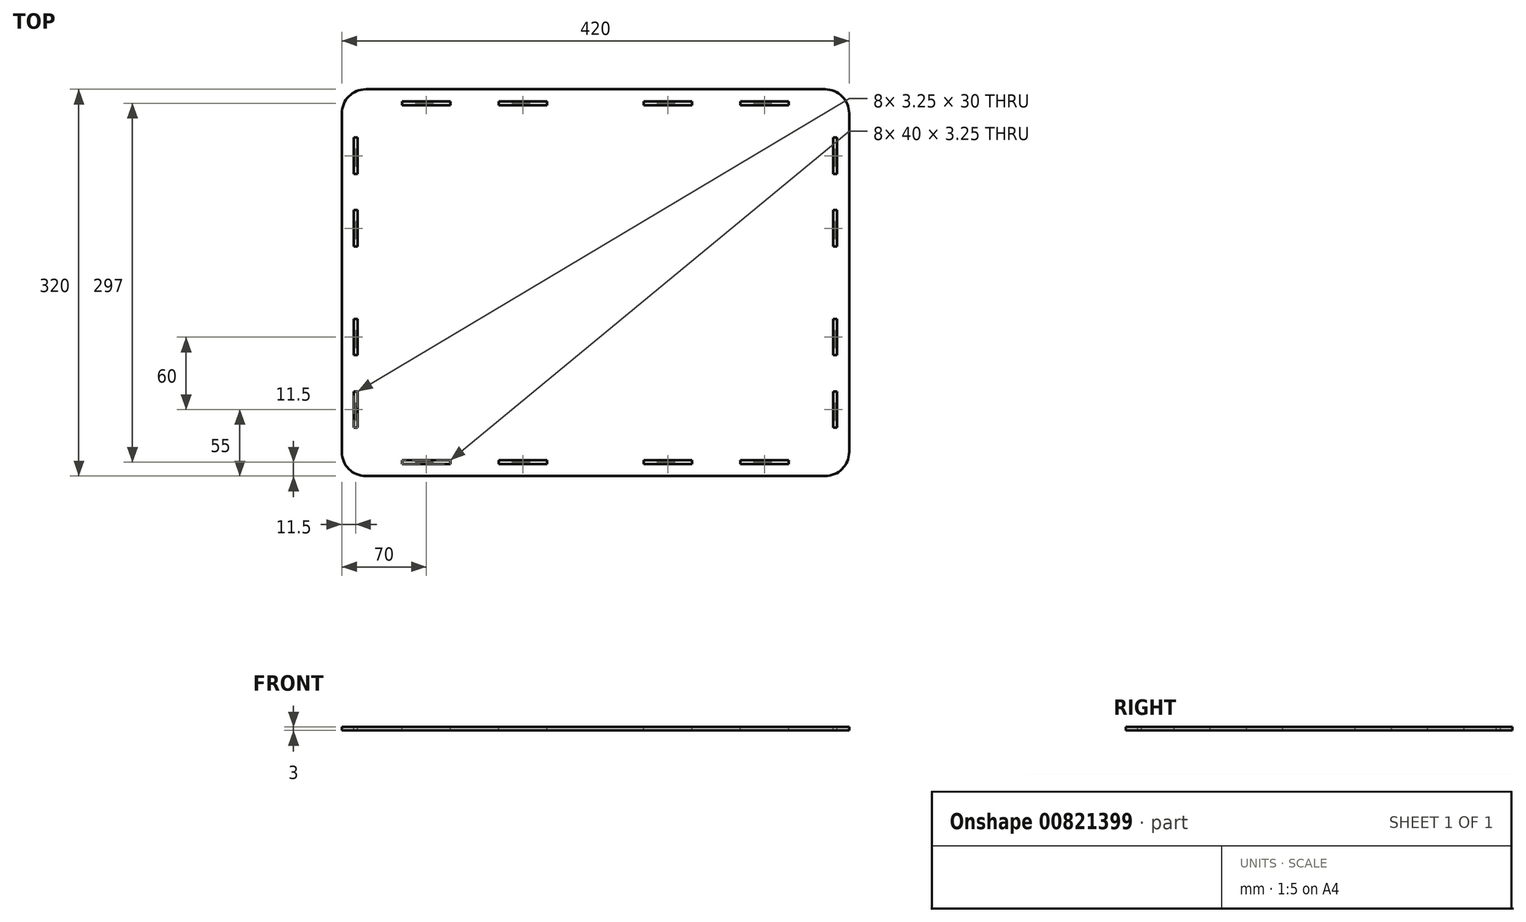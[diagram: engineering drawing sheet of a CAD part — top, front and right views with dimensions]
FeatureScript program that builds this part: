
annotation { "Feature Type Name" : "Feature", "Feature Type Description" : "" }
export const myFeature = defineFeature(function(context is Context, id is Id, definition is map)
    precondition{}
    {
        {
            var Q0;
            Q0=qCreatedBy(makeId("Top.planeOp"),FACE);
            var sketch = newSketch(context, id + "F0", { "sketchPlane" : qUnion([Q0])});
            skLineSegment(sketch, "E0.bottom", {"start": v(-190, 160) * mm, "end": v(190, 160) * mm});
            skLineSegment(sketch, "E0.top", {"start": v(-190, -160) * mm, "end": v(190, -160) * mm});
            skLineSegment(sketch, "E0.left", {"start": v(-210, 140) * mm, "end": v(-210, -140) * mm});
            skLineSegment(sketch, "E0.right", {"start": v(210, 140) * mm, "end": v(210, -140) * mm});
            skPoint(sketch, "E0.middle", {"position": v(0, 0) * mm});
            skPoint(sketch, "E1.visualSharp", {"position": v(210, 160) * mm});
            skArc(sketch, "E1.filletArc", {"start": v(210, 140) * mm, "mid": v(204.14, 154.14) * mm, "end": v(190, 160) * mm});
            skPoint(sketch, "E2.visualSharp", {"position": v(210, -160) * mm});
            skArc(sketch, "E2.filletArc", {"start": v(190, -160) * mm, "mid": v(204.14, -154.14) * mm, "end": v(210, -140) * mm});
            skPoint(sketch, "E3.visualSharp", {"position": v(-210, -160) * mm});
            skArc(sketch, "E3.filletArc", {"start": v(-210, -140) * mm, "mid": v(-204.14, -154.14) * mm, "end": v(-190, -160) * mm});
            skPoint(sketch, "E4.visualSharp", {"position": v(-210, 160) * mm});
            skArc(sketch, "E4.filletArc", {"start": v(-190, 160) * mm, "mid": v(-204.14, 154.14) * mm, "end": v(-210, 140) * mm});
            skSolve(sketch);
        }
        {
            var Q0;
            Q0=makeQuery(id+"F0.imprint","IMPRINT",FACE,{"disambiguationData":[TD([[makeQuery(id+"F0.imprint","IMPRINT",EDGE,{"derivedFrom":sQuery(id+"F0.wireOp",EDGE,"E0.bottom")}),-1.0]])]});
            extrude(context, id + "F1", {"entities" : qUnion([Q0]), "depth" : 3 * mm, "offsetDistance" : 25 * mm});
        }
        {
            var Q0;
            Q0=makeQuery(id+"F1.opExtrude","CAP_FACE",FACE,{"disambiguationData":[OSD([sQuery(id+"F0.wireOp",EDGE,"E0.bottom"),sQuery(id+"F0.wireOp",EDGE,"E0.top"),sQuery(id+"F0.wireOp",EDGE,"E0.left"),sQuery(id+"F0.wireOp",EDGE,"E0.right"),sQuery(id+"F0.wireOp",EDGE,"E1.filletArc"),sQuery(id+"F0.wireOp",EDGE,"E2.filletArc"),sQuery(id+"F0.wireOp",EDGE,"E3.filletArc"),sQuery(id+"F0.wireOp",EDGE,"E4.filletArc")])],"isStart":false});
            var sketch = newSketch(context, id + "F2", { "sketchPlane" : qUnion([Q0])});
            skPoint(sketch, "E5.middle", {"position": v(0, 0) * mm});
            skLineSegment(sketch, "E6.bottom", {"start": v(-200.13, -90) * mm, "end": v(-196.88, -90) * mm});
            skLineSegment(sketch, "E6.top", {"start": v(-200.13, -120) * mm, "end": v(-196.88, -120) * mm});
            skLineSegment(sketch, "E6.left", {"start": v(-200.13, -90) * mm, "end": v(-200.13, -120) * mm});
            skLineSegment(sketch, "E6.right", {"start": v(-196.88, -90) * mm, "end": v(-196.88, -120) * mm});
            skPoint(sketch, "E6.middle", {"position": v(-198.5, -105) * mm});
            skLineSegment(sketch, "E7.bottom", {"start": v(-196.88, -60) * mm, "end": v(-200.13, -60) * mm});
            skLineSegment(sketch, "E7.top", {"start": v(-196.88, -30) * mm, "end": v(-200.13, -30) * mm});
            skLineSegment(sketch, "E7.left", {"start": v(-196.88, -60) * mm, "end": v(-196.88, -30) * mm});
            skLineSegment(sketch, "E7.right", {"start": v(-200.13, -60) * mm, "end": v(-200.13, -30) * mm});
            skPoint(sketch, "E7.middle", {"position": v(-198.5, -45) * mm});
            skLineSegment(sketch, "E8.bottom", {"start": v(-120, -150.12) * mm, "end": v(-160, -150.12) * mm});
            skLineSegment(sketch, "E8.top", {"start": v(-120, -146.88) * mm, "end": v(-160, -146.88) * mm});
            skLineSegment(sketch, "E8.right", {"start": v(-160, -150.12) * mm, "end": v(-160, -146.87) * mm});
            skPoint(sketch, "E8.middle", {"position": v(-140, -148.5) * mm});
            skLineSegment(sketch, "E9.MirrorCS", {"start": v(-196.88, 30) * mm, "end": v(-200.13, 30) * mm});
            skLineSegment(sketch, "E10.MirrorCS", {"start": v(-200.13, 120) * mm, "end": v(-196.88, 120) * mm});
            skLineSegment(sketch, "E11.MirrorCS", {"start": v(-196.88, 60) * mm, "end": v(-200.13, 60) * mm});
            skLineSegment(sketch, "E12.MirrorCS", {"start": v(-200.13, 90) * mm, "end": v(-196.88, 90) * mm});
            skPoint(sketch, "E13.MirrorP", {"position": v(-198.5, 45) * mm});
            skPoint(sketch, "E14.MirrorP", {"position": v(-198.5, 105) * mm});
            skLineSegment(sketch, "E15.MirrorCS", {"start": v(-196.88, 60) * mm, "end": v(-196.88, 30) * mm});
            skLineSegment(sketch, "E16.MirrorCS", {"start": v(-196.88, 90) * mm, "end": v(-196.88, 120) * mm});
            skLineSegment(sketch, "E17.MirrorCS", {"start": v(-200.13, 90) * mm, "end": v(-200.13, 120) * mm});
            skLineSegment(sketch, "E18.MirrorCS", {"start": v(-200.13, 60) * mm, "end": v(-200.13, 30) * mm});
            skLineSegment(sketch, "E19", {"start": v(-120, -146.88) * mm, "end": v(-120, -150.12) * mm});
            skLineSegment(sketch, "E20.bottom", {"start": v(-40, -150.12) * mm, "end": v(-80, -150.12) * mm});
            skLineSegment(sketch, "E20.top", {"start": v(-40, -146.87) * mm, "end": v(-80, -146.87) * mm});
            skLineSegment(sketch, "E20.left", {"start": v(-40, -150.12) * mm, "end": v(-40, -146.87) * mm});
            skPoint(sketch, "E20.middle", {"position": v(-60, -148.5) * mm});
            skLineSegment(sketch, "E21", {"start": v(-80, -150.12) * mm, "end": v(-80, -146.87) * mm});
            skLineSegment(sketch, "E22.MirrorCS", {"start": v(160, -150.12) * mm, "end": v(160, -146.87) * mm});
            skLineSegment(sketch, "E23.MirrorCS", {"start": v(80, -150.12) * mm, "end": v(80, -146.87) * mm});
            skLineSegment(sketch, "E24.MirrorCS", {"start": v(120, -146.88) * mm, "end": v(120, -150.12) * mm});
            skLineSegment(sketch, "E25.MirrorCS", {"start": v(40, -150.12) * mm, "end": v(40, -146.87) * mm});
            skPoint(sketch, "E26.MirrorP", {"position": v(60, -148.5) * mm});
            skLineSegment(sketch, "E27.MirrorCS", {"start": v(40, -150.12) * mm, "end": v(80, -150.12) * mm});
            skLineSegment(sketch, "E28.MirrorCS", {"start": v(40, -146.87) * mm, "end": v(80, -146.87) * mm});
            skPoint(sketch, "E29.MirrorP", {"position": v(140, -148.5) * mm});
            skLineSegment(sketch, "E30.MirrorCS", {"start": v(120, -146.88) * mm, "end": v(160, -146.88) * mm});
            skLineSegment(sketch, "E31.MirrorCS", {"start": v(120, -150.12) * mm, "end": v(160, -150.12) * mm});
            skLineSegment(sketch, "E32.MirrorCS", {"start": v(160, 150.12) * mm, "end": v(160, 146.87) * mm});
            skLineSegment(sketch, "E33.MirrorCS", {"start": v(40, 150.12) * mm, "end": v(40, 146.87) * mm});
            skLineSegment(sketch, "E34.MirrorCS", {"start": v(-160, 150.12) * mm, "end": v(-160, 146.87) * mm});
            skLineSegment(sketch, "E35.MirrorCS", {"start": v(-80, 150.12) * mm, "end": v(-80, 146.87) * mm});
            skLineSegment(sketch, "E36.MirrorCS", {"start": v(120, 146.88) * mm, "end": v(120, 150.12) * mm});
            skLineSegment(sketch, "E37.MirrorCS", {"start": v(-120, 146.88) * mm, "end": v(-120, 150.12) * mm});
            skLineSegment(sketch, "E38.MirrorCS", {"start": v(-40, 150.12) * mm, "end": v(-40, 146.87) * mm});
            skLineSegment(sketch, "E39.MirrorCS", {"start": v(80, 150.12) * mm, "end": v(80, 146.87) * mm});
            skPoint(sketch, "E40.MirrorP", {"position": v(-60, 148.5) * mm});
            skLineSegment(sketch, "E41.MirrorCS", {"start": v(40, 150.12) * mm, "end": v(80, 150.12) * mm});
            skPoint(sketch, "E42.MirrorP", {"position": v(140, 148.5) * mm});
            skPoint(sketch, "E43.MirrorP", {"position": v(60, 148.5) * mm});
            skLineSegment(sketch, "E44.MirrorCS", {"start": v(120, 146.88) * mm, "end": v(160, 146.88) * mm});
            skLineSegment(sketch, "E45.MirrorCS", {"start": v(-120, 146.88) * mm, "end": v(-160, 146.88) * mm});
            skLineSegment(sketch, "E46.MirrorCS", {"start": v(-40, 146.87) * mm, "end": v(-80, 146.87) * mm});
            skPoint(sketch, "E47.MirrorP", {"position": v(-140, 148.5) * mm});
            skLineSegment(sketch, "E48.MirrorCS", {"start": v(-120, 150.12) * mm, "end": v(-160, 150.12) * mm});
            skLineSegment(sketch, "E49.MirrorCS", {"start": v(40, 146.87) * mm, "end": v(80, 146.87) * mm});
            skLineSegment(sketch, "E50.MirrorCS", {"start": v(-40, 150.12) * mm, "end": v(-80, 150.12) * mm});
            skLineSegment(sketch, "E51.MirrorCS", {"start": v(120, 150.12) * mm, "end": v(160, 150.12) * mm});
            skLineSegment(sketch, "E52.MirrorCS", {"start": v(196.88, -60) * mm, "end": v(200.13, -60) * mm});
            skLineSegment(sketch, "E53.MirrorCS", {"start": v(196.88, -30) * mm, "end": v(200.13, -30) * mm});
            skLineSegment(sketch, "E54.MirrorCS", {"start": v(196.88, 60) * mm, "end": v(200.13, 60) * mm});
            skLineSegment(sketch, "E55.MirrorCS", {"start": v(200.13, 120) * mm, "end": v(196.88, 120) * mm});
            skLineSegment(sketch, "E56.MirrorCS", {"start": v(200.13, -120) * mm, "end": v(196.88, -120) * mm});
            skLineSegment(sketch, "E57.MirrorCS", {"start": v(200.13, -90) * mm, "end": v(196.88, -90) * mm});
            skLineSegment(sketch, "E58.MirrorCS", {"start": v(196.88, 30) * mm, "end": v(200.13, 30) * mm});
            skLineSegment(sketch, "E59.MirrorCS", {"start": v(200.13, 90) * mm, "end": v(196.88, 90) * mm});
            skLineSegment(sketch, "E60.MirrorCS", {"start": v(196.88, -60) * mm, "end": v(196.88, -30) * mm});
            skLineSegment(sketch, "E61.MirrorCS", {"start": v(196.88, 60) * mm, "end": v(196.88, 30) * mm});
            skLineSegment(sketch, "E62.MirrorCS", {"start": v(200.13, -90) * mm, "end": v(200.13, -120) * mm});
            skLineSegment(sketch, "E63.MirrorCS", {"start": v(200.13, 90) * mm, "end": v(200.13, 120) * mm});
            skLineSegment(sketch, "E64.MirrorCS", {"start": v(200.13, 60) * mm, "end": v(200.13, 30) * mm});
            skLineSegment(sketch, "E65.MirrorCS", {"start": v(200.13, -60) * mm, "end": v(200.13, -30) * mm});
            skLineSegment(sketch, "E66.MirrorCS", {"start": v(196.88, 90) * mm, "end": v(196.88, 120) * mm});
            skLineSegment(sketch, "E67.MirrorCS", {"start": v(196.88, -90) * mm, "end": v(196.88, -120) * mm});
            skPoint(sketch, "E68.MirrorP", {"position": v(198.5, 105) * mm});
            skPoint(sketch, "E69.MirrorP", {"position": v(198.5, 45) * mm});
            skPoint(sketch, "E70.MirrorP", {"position": v(198.5, -105) * mm});
            skPoint(sketch, "E71.MirrorP", {"position": v(198.5, -45) * mm});
            skSolve(sketch);
        }
        {
            var Q0;
            Q0=makeQuery(id+"F2.imprint","IMPRINT",FACE,{"disambiguationData":[TD([[makeQuery(id+"F2.imprint","IMPRINT",EDGE,{"derivedFrom":sQuery(id+"F2.wireOp",EDGE,"E34.MirrorCS")}),1.0]])]});
            var Q1;
            Q1=makeQuery(id+"F2.imprint","IMPRINT",FACE,{"disambiguationData":[TD([[makeQuery(id+"F2.imprint","IMPRINT",EDGE,{"derivedFrom":sQuery(id+"F2.wireOp",EDGE,"E35.MirrorCS")}),1.0]])]});
            var Q2;
            Q2=makeQuery(id+"F2.imprint","IMPRINT",FACE,{"disambiguationData":[TD([[makeQuery(id+"F2.imprint","IMPRINT",EDGE,{"derivedFrom":sQuery(id+"F2.wireOp",EDGE,"E33.MirrorCS")}),1.0]])]});
            var Q3;
            Q3=makeQuery(id+"F2.imprint","IMPRINT",FACE,{"disambiguationData":[TD([[makeQuery(id+"F2.imprint","IMPRINT",EDGE,{"derivedFrom":sQuery(id+"F2.wireOp",EDGE,"E32.MirrorCS")}),-1.0]])]});
            var Q4;
            Q4=makeQuery(id+"F2.imprint","IMPRINT",FACE,{"disambiguationData":[TD([[makeQuery(id+"F2.imprint","IMPRINT",EDGE,{"derivedFrom":sQuery(id+"F2.wireOp",EDGE,"E55.MirrorCS")}),1.0]])]});
            var Q5;
            Q5=makeQuery(id+"F2.imprint","IMPRINT",FACE,{"disambiguationData":[TD([[makeQuery(id+"F2.imprint","IMPRINT",EDGE,{"derivedFrom":sQuery(id+"F2.wireOp",EDGE,"E54.MirrorCS")}),-1.0]])]});
            var Q6;
            Q6=makeQuery(id+"F2.imprint","IMPRINT",FACE,{"disambiguationData":[TD([[makeQuery(id+"F2.imprint","IMPRINT",EDGE,{"derivedFrom":sQuery(id+"F2.wireOp",EDGE,"E52.MirrorCS")}),1.0]])]});
            var Q7;
            Q7=makeQuery(id+"F2.imprint","IMPRINT",FACE,{"disambiguationData":[TD([[makeQuery(id+"F2.imprint","IMPRINT",EDGE,{"derivedFrom":sQuery(id+"F2.wireOp",EDGE,"E10.MirrorCS")}),-1.0]])]});
            var Q8;
            Q8=makeQuery(id+"F2.imprint","IMPRINT",FACE,{"disambiguationData":[TD([[makeQuery(id+"F2.imprint","IMPRINT",EDGE,{"derivedFrom":sQuery(id+"F2.wireOp",EDGE,"E9.MirrorCS")}),-1.0]])]});
            var Q9;
            Q9=makeQuery(id+"F2.imprint","IMPRINT",FACE,{"disambiguationData":[TD([[makeQuery(id+"F2.imprint","IMPRINT",EDGE,{"derivedFrom":sQuery(id+"F2.wireOp",EDGE,"E7.bottom")}),-1.0]])]});
            var Q10;
            Q10=makeQuery(id+"F2.imprint","IMPRINT",FACE,{"disambiguationData":[TD([[makeQuery(id+"F2.imprint","IMPRINT",EDGE,{"derivedFrom":sQuery(id+"F2.wireOp",EDGE,"E6.bottom")}),-1.0]])]});
            var Q11;
            Q11=makeQuery(id+"F2.imprint","IMPRINT",FACE,{"disambiguationData":[TD([[makeQuery(id+"F2.imprint","IMPRINT",EDGE,{"derivedFrom":sQuery(id+"F2.wireOp",EDGE,"E8.bottom")}),-1.0]])]});
            var Q12;
            Q12=makeQuery(id+"F2.imprint","IMPRINT",FACE,{"disambiguationData":[TD([[makeQuery(id+"F2.imprint","IMPRINT",EDGE,{"derivedFrom":sQuery(id+"F2.wireOp",EDGE,"E20.bottom")}),-1.0]])]});
            var Q13;
            Q13=makeQuery(id+"F2.imprint","IMPRINT",FACE,{"disambiguationData":[TD([[makeQuery(id+"F2.imprint","IMPRINT",EDGE,{"derivedFrom":sQuery(id+"F2.wireOp",EDGE,"E23.MirrorCS")}),1.0]])]});
            var Q14;
            Q14=makeQuery(id+"F2.imprint","IMPRINT",FACE,{"disambiguationData":[TD([[makeQuery(id+"F2.imprint","IMPRINT",EDGE,{"derivedFrom":sQuery(id+"F2.wireOp",EDGE,"E22.MirrorCS")}),1.0]])]});
            var Q15;
            Q15=makeQuery(id+"F2.imprint","IMPRINT",FACE,{"disambiguationData":[TD([[makeQuery(id+"F2.imprint","IMPRINT",EDGE,{"derivedFrom":sQuery(id+"F2.wireOp",EDGE,"E56.MirrorCS")}),-1.0]])]});
            extrude(context, id + "F3", {"entities" : qUnion([Q0, Q1, Q2, Q3, Q4, Q5, Q6, Q7, Q8, Q9, Q10, Q11, Q12, Q13, Q14, Q15]), "operationType" : NewBodyOperationType.REMOVE, "oppositeDirection" : true, "depth" : 3 * mm, "offsetDistance" : 25 * mm});
        }
    });
